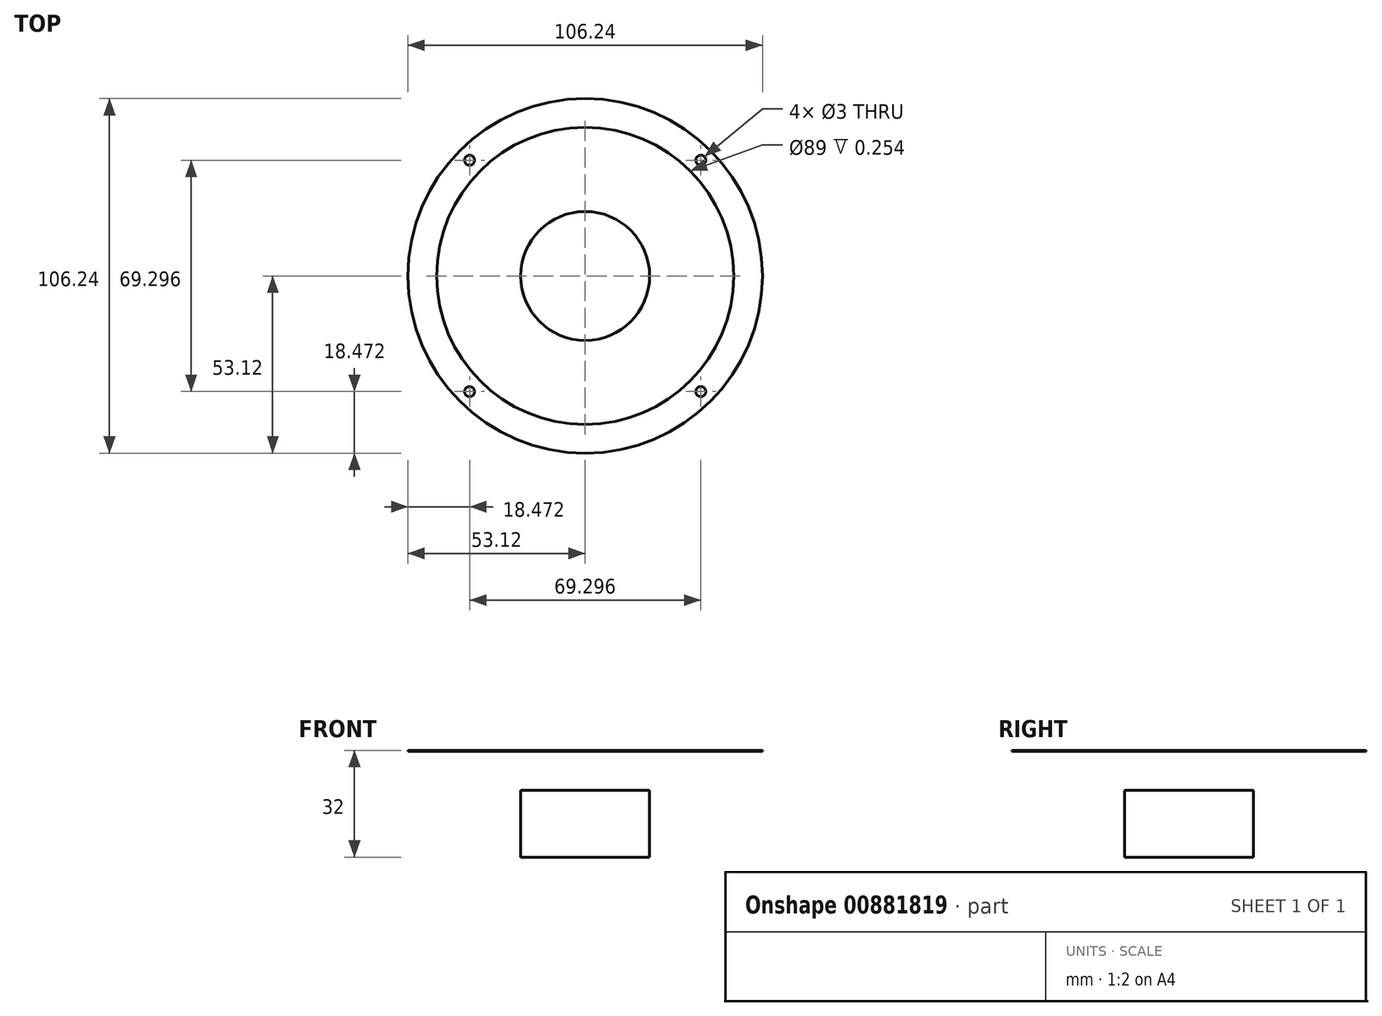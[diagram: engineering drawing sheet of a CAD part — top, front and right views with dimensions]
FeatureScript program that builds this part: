
annotation { "Feature Type Name" : "Feature", "Feature Type Description" : "" }
export const myFeature = defineFeature(function(context is Context, id is Id, definition is map)
    precondition{}
    {
        {
            var Q0;
            Q0=qCreatedBy(makeId("Front.planeOp"),FACE);
            var sketch = newSketch(context, id + "F0", { "sketchPlane" : qUnion([Q0])});
            skFitSpline(sketch, "E0", {"points": [v(-16.45, 0) * mm, v(0, 6.75) * mm], "startDerivative": vector(0, 9.42) * mm, "endDerivative": vector(28.82, 0) * mm});
            skLineSegment(sketch, "E1", {"start": v(0, 20.33) * mm, "end": v(0, 0) * mm, "construction": true});
            skArc(sketch, "E2", {"start": v(-35.5, 12) * mm, "mid": v(-40, 19.18) * mm, "end": v(-44.5, 12) * mm});
            skLineSegment(sketch, "E3", {"start": v(-16.45, 0) * mm, "end": v(-19.3, 0) * mm});
            skLineSegment(sketch, "E4", {"start": v(-19.3, 0) * mm, "end": v(-35.5, 12) * mm});
            skLineSegment(sketch, "E5.bottom", {"start": v(0, 0) * mm, "end": v(-19.3, 0) * mm});
            skLineSegment(sketch, "E5.top", {"start": v(0, -20) * mm, "end": v(-19.3, -20) * mm});
            skLineSegment(sketch, "E5.left", {"start": v(0, 0) * mm, "end": v(0, -20) * mm});
            skLineSegment(sketch, "E5.right", {"start": v(-19.3, 0) * mm, "end": v(-19.3, -20) * mm});
            skLineSegment(sketch, "E6.bottom", {"start": v(-44.5, 12) * mm, "end": v(-53.12, 12) * mm});
            skLineSegment(sketch, "E6.top", {"start": v(-44.5, 11.75) * mm, "end": v(-53.12, 11.75) * mm});
            skLineSegment(sketch, "E6.left", {"start": v(-44.5, 12) * mm, "end": v(-44.5, 11.75) * mm});
            skLineSegment(sketch, "E6.right", {"start": v(-53.12, 12) * mm, "end": v(-53.12, 11.75) * mm});
            skSolve(sketch);
        }
        {
            var Q0;
            Q0=makeQuery(id+"F0.imprint","IMPRINT",FACE,{"disambiguationData":[TD([[makeQuery(id+"F0.imprint","IMPRINT",EDGE,{"derivedFrom":sQuery(id+"F0.wireOp",EDGE,"8bf1bfcc-ef00-45cb-b3df-b8ebd05150fe.0.endCap")}),-1.0]])]});
            var Q1;
            Q1=sQuery(id+"F0.wireOp",EDGE,"E2");
            var Q2;
            Q2=sQuery(id+"F0.wireOp",EDGE,"E0");
            var Q3;
            Q3=sQuery(id+"F0.wireOp",EDGE,"E1");
            revolve(context, id + "F1", {"bodyType" : ToolBodyType.SURFACE, "surfaceOperationType" : NewSurfaceOperationType.NEW, "entities" : qUnion([Q0]), "surfaceEntities" : qUnion([Q1, Q2]), "axis" : qUnion([Q3]), "revolveType" : RevolveType.FULL});
        }
        {
            var Q0;
            Q0=sQuery(id+"F0.wireOp",EDGE,"E4");
            var Q1;
            Q1=sQuery(id+"F0.wireOp",EDGE,"E1");
            revolve(context, id + "F2", {"bodyType" : ToolBodyType.SURFACE, "operationType" : NewBodyOperationType.ADD, "surfaceOperationType" : NewSurfaceOperationType.ADD, "surfaceEntities" : qUnion([Q0]), "axis" : qUnion([Q1]), "revolveType" : RevolveType.FULL});
        }
        {
            var Q0;
            Q0=makeQuery(id+"F0.imprint","IMPRINT",FACE,{"disambiguationData":[TD([[makeQuery(id+"F0.imprint","IMPRINT",EDGE,{"derivedFrom":sQuery(id+"F0.wireOp",EDGE,"E5.top")}),-1.0]])]});
            var Q1;
            Q1=makeQuery(id+"F0.imprint","IMPRINT",FACE,{"disambiguationData":[TD([[makeQuery(id+"F0.imprint","IMPRINT",EDGE,{"derivedFrom":sQuery(id+"F0.wireOp",EDGE,"E6.bottom")}),1.0]])]});
            var Q2;
            Q2=sQuery(id+"F0.wireOp",EDGE,"E1");
            revolve(context, id + "F3", {"surfaceOperationType" : NewSurfaceOperationType.NEW, "entities" : qUnion([Q0, Q1]), "axis" : qUnion([Q2]), "revolveType" : RevolveType.FULL});
        }
        {
            var Q0;
            Q0=makeQuery(id+"F1.opRevolve","SWEPT_FACE",FACE,{"disambiguationData":[OSD([sQuery(id+"F0.wireOp",EDGE,"MtWVmWCX-k4Ll-qhs3-tkXD-c6KtTaQjciUn")])]});
            var Q1;
            Q1=makeQuery(id+"F3.opRevolve","SWEPT_FACE",FACE,{"disambiguationData":[OSD([sQuery(id+"F0.wireOp",EDGE,"E6.bottom")])]});
            cPlane(context, id + "F4", {"entities" : qUnion([Q0, Q1]), "cplaneType" : CPlaneType.OFFSET, "offset" : 0 * mm, "width" : 150 * mm, "height" : 150 * mm});
        }
        {
            var Q0;
            Q0=qCreatedBy(id+"F4.planeOp",FACE);
            var sketch = newSketch(context, id + "F5", { "sketchPlane" : qUnion([Q0])});
            skLineSegment(sketch, "E7", {"start": v(0, 0) * mm, "end": v(-34.65, 34.65) * mm, "construction": true});
            skLineSegment(sketch, "E8.MirrorCS", {"start": v(0, 0) * mm, "end": v(34.65, 34.65) * mm, "construction": true});
            skLineSegment(sketch, "E9.MirrorCS", {"start": v(0, 0) * mm, "end": v(34.65, -34.65) * mm, "construction": true});
            skLineSegment(sketch, "E10.MirrorCS", {"start": v(0, 0) * mm, "end": v(-34.65, -34.65) * mm, "construction": true});
            skSolve(sketch);
        }
        {
            var Q0;
            Q0=sQuery(id+"F5.wireOp",VERTEX,"E7.end");
            var Q1;
            Q1=sQuery(id+"F5.wireOp",VERTEX,"9f6357c5-e04f-4bf7-9c00-211f84f4a0ef0.MirrorC.center");
            var Q2;
            Q2=sQuery(id+"F5.wireOp",VERTEX,"251eb548-a396-41da-8fe7-84cc026d53c90.MirrorC.center");
            var Q3;
            Q3=sQuery(id+"F5.wireOp",VERTEX,"48249fb2-1a4f-4c4c-b1bf-f230d80eff100.MirrorC.center");
            var Q4;
            Q4=sQuery(id+"F5.wireOp",VERTEX,"E8.MirrorCS.end");
            var Q5;
            Q5=sQuery(id+"F5.wireOp",VERTEX,"E9.MirrorCS.end");
            var Q6;
            Q6=sQuery(id+"F5.wireOp",VERTEX,"E10.MirrorCS.end");
            var Q7;
            Q7=makeQuery(id+"F3.opRevolve","SWEPT_BODY",BODY,{"disambiguationData":[OSD([sQuery(id+"F0.wireOp",EDGE,"E6.bottom"),sQuery(id+"F0.wireOp",EDGE,"E6.top"),sQuery(id+"F0.wireOp",EDGE,"E6.left"),sQuery(id+"F0.wireOp",EDGE,"E6.right")])]});
            hole(context, id + "F6", {"style" : HoleStyle.SIMPLE, "endStyle" : HoleEndStyle.THROUGH, "holeDiameter" : 3 * mm, "majorDiameter" : 5 * mm, "isTappedThrough" : true, "tappedDepth" : 12 * mm, "tapClearance" : 3, "startFromSketch" : true, "locations" : qUnion([Q0, Q1, Q2, Q3, Q4, Q5, Q6]), "scope" : qUnion([Q7])});
        }
    });
